# Revit family: Circular_Side_Table_BIM
name_source: partatom
category: Arredi
units: mm (PartAtom-declared; Revit-internal decimal feet)

## family parameters
Attiva taglio nelle viste = No
Basato su piano di lavoro = No
Condiviso = No
Numero OmniClass = 23.40.20.00
Origine composizione di rendering = Geometria famiglia
Punto di calcolo locali = No
Sempre verticale = Sì
Taglio con vuoti quando caricato = No
Titolo OmniClass = General Furniture and Specialties

## types (1)
- CB-3717
    AVAILABLE FINISHES = Ebonized black lacquer on Ash (EB) or bleached, white pigment, matte acrylic on Ash (BL). Raw effect lacquer on Oak (RE). Hand rubbed natural oil on Oak or Walnut (NA), or hand rubbed black oil on Walnut (BO).
    BASE MATERIAL = BASSAM_FELLOWS_OAK_O-NA
    BIM BADGE = https://bim.archiproducts.com
    COLLECTION = CIRCULAR
    DIAMETER = 400 mm  [stored 1.31234 ft]
    Descrizione = Round stainless steel and wood side table
    HEIGHT = 400 mm  [stored 1.31234 ft]
    MATERIAL DESCRIPTION = Solid wood top, tubular stainless steel base.
    Modello = Circular Side Table
    PRODUCT CODE = CB-3717
    PRODUCT SHEET = https://www.archiproducts.com
    Produttore = BassamFellows
    Prospetto di default = 0 mm  [stored 0 ft]
    STRUCTURE MATERIAL = BASSAM_FELLOWS_MATT_BLACK_BP
    TECHNICAL SHEET = https://bassamfellows.com
    URL = https://bassamfellows.com

note: [stored X ft] marks values corroborated as IEEE doubles in the binary element streams (Revit-internal decimal feet)

## geometry (parser evidence)
native form markers: Sweep x3
no freeform markers — native parametric forms only
